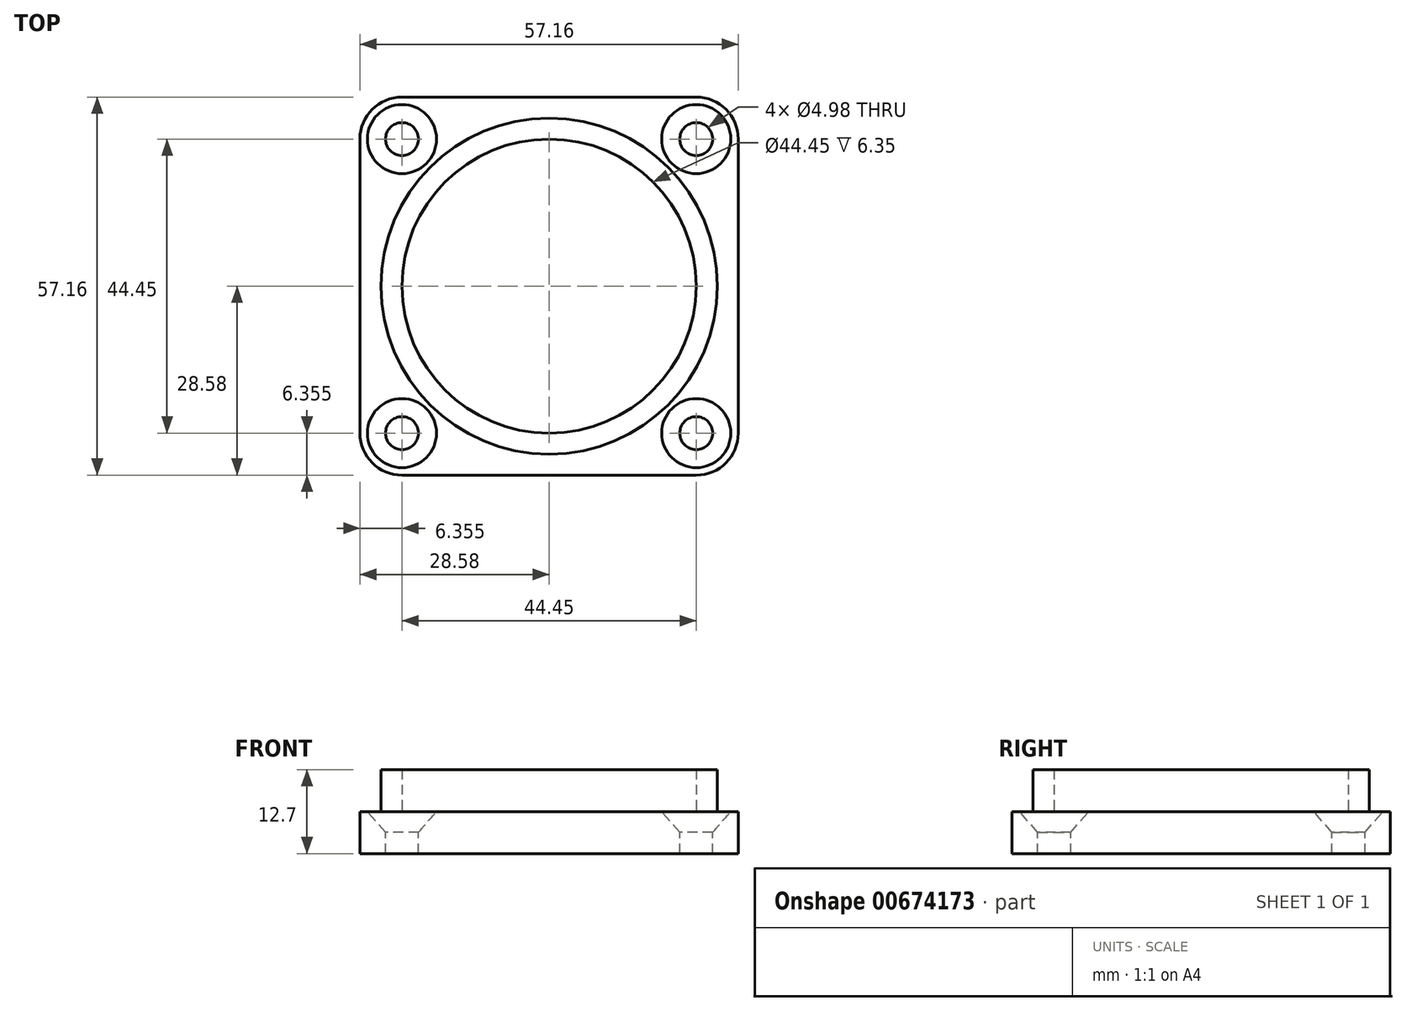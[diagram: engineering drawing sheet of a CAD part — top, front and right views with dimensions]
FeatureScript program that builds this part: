
annotation { "Feature Type Name" : "Feature", "Feature Type Description" : "" }
export const myFeature = defineFeature(function(context is Context, id is Id, definition is map)
    precondition{}
    {
        {
            var Q0;
            Q0=qCreatedBy(makeId("Top.planeOp"),FACE);
            var sketch = newSketch(context, id + "F0", { "sketchPlane" : qUnion([Q0])});
            skLineSegment(sketch, "E0.bottom", {"start": v(28.57, -28.58) * mm, "end": v(-28.58, -28.58) * mm});
            skLineSegment(sketch, "E0.top", {"start": v(28.58, 28.58) * mm, "end": v(-28.58, 28.58) * mm});
            skLineSegment(sketch, "E0.left", {"start": v(28.57, -28.58) * mm, "end": v(28.58, 28.58) * mm});
            skLineSegment(sketch, "E0.right", {"start": v(-28.58, -28.58) * mm, "end": v(-28.58, 28.57) * mm});
            skPoint(sketch, "E0.middle", {"position": v(0, 0) * mm});
            skSolve(sketch);
        }
        {
            var Q0;
            Q0 = qSketchRegion(id + "F0", true);
            extrude(context, id + "F1", {"entities" : qUnion([Q0]), "depth" : 6.35 * mm, "offsetDistance" : 25.4 * mm});
        }
        {
            var Q0;
            Q0=makeQuery(id+"F1.opExtrude","CAP_FACE",FACE,{"disambiguationData":[OSD([sQuery(id+"F0.wireOp",EDGE,"E0.bottom"),sQuery(id+"F0.wireOp",EDGE,"E0.top"),sQuery(id+"F0.wireOp",EDGE,"E0.left"),sQuery(id+"F0.wireOp",EDGE,"E0.right")])],"isStart":false});
            var sketch = newSketch(context, id + "F2", { "sketchPlane" : qUnion([Q0])});
            skLineSegment(sketch, "E1.bottom", {"start": v(22.23, 22.23) * mm, "end": v(-22.23, 22.23) * mm});
            skLineSegment(sketch, "E1.top", {"start": v(22.23, -22.23) * mm, "end": v(-22.23, -22.23) * mm});
            skLineSegment(sketch, "E1.left", {"start": v(22.23, 22.23) * mm, "end": v(22.23, -22.23) * mm});
            skLineSegment(sketch, "E1.right", {"start": v(-22.23, 22.23) * mm, "end": v(-22.23, -22.23) * mm});
            skPoint(sketch, "E1.middle", {"position": v(0, 0) * mm});
            skPoint(sketch, "E2", {"position": v(-22.23, 22.23) * mm});
            skPoint(sketch, "E3", {"position": v(22.23, 22.23) * mm});
            skPoint(sketch, "E4", {"position": v(22.23, -22.23) * mm});
            skPoint(sketch, "E5", {"position": v(-22.23, -22.23) * mm});
            skSolve(sketch);
        }
        {
            var Q0;
            Q0=sQuery(id+"F2.wireOp",VERTEX,"8928b8e4-04ff-4a8b-a7c0-791953d7a321");
            var Q1;
            Q1=sQuery(id+"F2.wireOp",VERTEX,"7caa15a3-8fe6-43bc-8db0-7b6654835b2a");
            var Q2;
            Q2=sQuery(id+"F2.wireOp",VERTEX,"c24be36a-aee6-45a9-b33d-e924ac05f89b");
            var Q3;
            Q3=sQuery(id+"F2.wireOp",VERTEX,"681f082f-101e-4ec8-9dc0-49ddf14968fd");
            var Q4;
            Q4=sQuery(id+"F2.wireOp",VERTEX,"E2");
            var Q5;
            Q5=sQuery(id+"F2.wireOp",VERTEX,"E3");
            var Q6;
            Q6=sQuery(id+"F2.wireOp",VERTEX,"E4");
            var Q7;
            Q7=sQuery(id+"F2.wireOp",VERTEX,"E5");
            var Q8;
            Q8=makeQuery(id+"F1.opExtrude","SWEPT_BODY",BODY,{"disambiguationData":[OSD([sQuery(id+"F0.wireOp",EDGE,"E0.bottom"),sQuery(id+"F0.wireOp",EDGE,"E0.top"),sQuery(id+"F0.wireOp",EDGE,"E0.left"),sQuery(id+"F0.wireOp",EDGE,"E0.right")])]});
            hole(context, id + "F3", {"style" : HoleStyle.C_SINK, "endStyle" : HoleEndStyle.THROUGH, "standardTappedOrClearance" : lookupTablePath({ "standard" : "ANSI", "fit" : "Close", "size" : "#10", "type" : "Clearance" }), "standardBlindInLast" : lookupTablePath({ "fit" : "Close", "standard" : "ANSI", "size" : "#10", "type" : "Clearance" }), "holeDiameter" : 4.98 * mm, "cSinkDiameter" : 10.44 * mm, "cSinkAngle" : 82 * degree, "majorDiameter" : 6.35 * mm, "isTappedThrough" : true, "tappedDepth" : 12.7 * mm, "tapClearance" : 3, "locations" : qUnion([Q0, Q1, Q2, Q3, Q4, Q5, Q6, Q7]), "scope" : qUnion([Q8])});
        }
        {
            var Q0;
            Q0=makeQuery(id+"F1.opExtrude","CAP_FACE",FACE,{"disambiguationData":[OSD([sQuery(id+"F0.wireOp",EDGE,"E0.bottom"),sQuery(id+"F0.wireOp",EDGE,"E0.top"),sQuery(id+"F0.wireOp",EDGE,"E0.left"),sQuery(id+"F0.wireOp",EDGE,"E0.right")])],"isStart":false});
            var sketch = newSketch(context, id + "F4", { "sketchPlane" : qUnion([Q0])});
            skCircle(sketch, "E6", {"center": v(0, 0) * mm, "radius": 22.23 * mm});
            skCircle(sketch, "E7.0", {"center": v(0, 0) * mm, "radius": 25.4 * mm});
            skLineSegment(sketch, "E8.0", {"start": v(34.93, -34.93) * mm, "end": v(34.93, 34.93) * mm});
            skLineSegment(sketch, "E8.1", {"start": v(-34.93, -34.93) * mm, "end": v(34.92, -34.93) * mm});
            skLineSegment(sketch, "E8.2", {"start": v(-34.93, 34.93) * mm, "end": v(-34.93, -34.93) * mm});
            skLineSegment(sketch, "E8.3", {"start": v(34.93, 34.93) * mm, "end": v(-34.92, 34.93) * mm});
            skSolve(sketch);
        }
        {
            var Q0;
            Q0=makeQuery(id+"F4.imprint","IMPRINT",FACE,{"disambiguationData":[TD([[makeQuery(id+"F4.imprint","IMPRINT",EDGE,{"derivedFrom":sQuery(id+"F4.wireOp",EDGE,"E6")}),-1.0]])]});
            var Q1;
            Q1=sQuery(id+"F4.wireOp",EDGE,"E7.0");
            var Q2;
            Q2=sQuery(id+"F4.wireOp",EDGE,"E6");
            extrude(context, id + "F5", {"entities" : qUnion([Q0]), "operationType" : NewBodyOperationType.ADD, "surfaceEntities" : qUnion([Q1, Q2]), "depth" : 6.35 * mm, "offsetDistance" : 25.4 * mm});
        }
        {
            var Q0;
            Q0=makeQuery(id+"F1.opExtrude","SWEPT_EDGE",EDGE,{"disambiguationData":[OSD([sQuery(id+"F0.wireOp",EDGE,"E0.top"),sQuery(id+"F0.wireOp",EDGE,"E0.left")])]});
            var Q1;
            Q1=makeQuery(id+"F1.opExtrude","SWEPT_EDGE",EDGE,{"disambiguationData":[OSD([sQuery(id+"F0.wireOp",EDGE,"E0.top"),sQuery(id+"F0.wireOp",EDGE,"E0.right")])]});
            var Q2;
            Q2=makeQuery(id+"F1.opExtrude","SWEPT_EDGE",EDGE,{"disambiguationData":[OSD([sQuery(id+"F0.wireOp",EDGE,"E0.bottom"),sQuery(id+"F0.wireOp",EDGE,"E0.left")])]});
            var Q3;
            Q3=makeQuery(id+"F1.opExtrude","SWEPT_EDGE",EDGE,{"disambiguationData":[OSD([sQuery(id+"F0.wireOp",EDGE,"E0.bottom"),sQuery(id+"F0.wireOp",EDGE,"E0.right")])]});
            fillet(context, id + "F6", {"entities" : qUnion([Q0, Q1, Q2, Q3]), "radius" : 6.35 * mm, "tangentPropagation" : true, "allowEdgeOverflow" : false});
        }
    });
